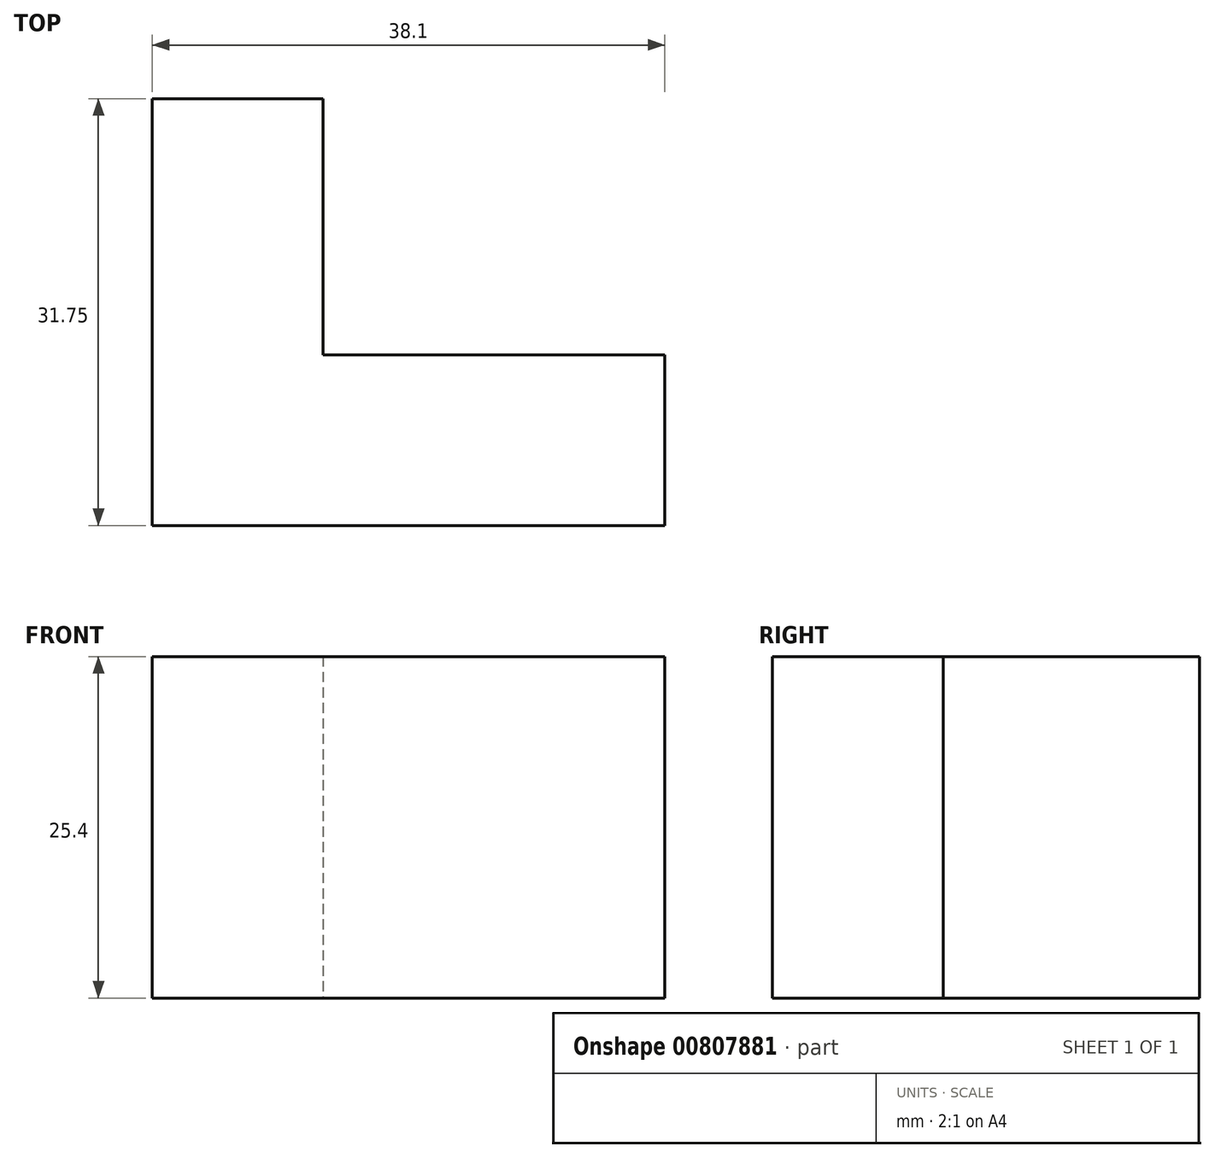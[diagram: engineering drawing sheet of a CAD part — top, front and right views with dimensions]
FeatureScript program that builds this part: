
annotation { "Feature Type Name" : "Feature", "Feature Type Description" : "" }
export const myFeature = defineFeature(function(context is Context, id is Id, definition is map)
    precondition{}
    {
        {
            var Q0;
            Q0=qCreatedBy(makeId("Top.planeOp"),FACE);
            var sketch = newSketch(context, id + "F0", { "sketchPlane" : qUnion([Q0])});
            skLineSegment(sketch, "E0", {"start": v(0, 0) * mm, "end": v(0, 31.75) * mm});
            skLineSegment(sketch, "E1", {"start": v(0, 31.75) * mm, "end": v(12.7, 31.75) * mm});
            skLineSegment(sketch, "E2", {"start": v(0, 0) * mm, "end": v(38.1, 0) * mm});
            skLineSegment(sketch, "E3", {"start": v(38.1, 0) * mm, "end": v(38.1, 12.7) * mm});
            skLineSegment(sketch, "E4", {"start": v(12.7, 31.75) * mm, "end": v(12.7, 12.7) * mm});
            skLineSegment(sketch, "E5", {"start": v(12.7, 12.7) * mm, "end": v(38.1, 12.7) * mm});
            skLineSegment(sketch, "E6", {"start": v(-112.42, -33.65) * mm, "end": v(-144.36, 12.7) * mm});
            skSolve(sketch);
        }
        {
            var Q0;
            Q0=makeQuery(id+"F0.imprint","IMPRINT",FACE,{"disambiguationData":[TD([[makeQuery(id+"F0.imprint","IMPRINT",EDGE,{"derivedFrom":sQuery(id+"F0.wireOp",EDGE,"E0")}),-1.0]])]});
            extrude(context, id + "F1", {"entities" : qUnion([Q0]), "depth" : 25.4 * mm, "offsetDistance" : 25.4 * mm});
        }
    });
